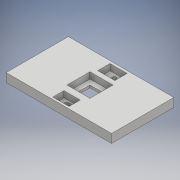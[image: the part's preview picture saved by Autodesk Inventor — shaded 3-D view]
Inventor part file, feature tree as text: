
AUTODESK INVENTOR PART (.ipt)
format: ipt  version: 2017 (Build 210142000, 142)  size: 321,024 bytes
history: native  units: mm
features: extrude x2, sketch x1
ambient origin geometry x8: Origin, YZ Plane, XZ Plane, XY Plane, X Axis, Y Axis, Z Axis, Center Point
bodies: Solido1 (feature_tree)
feature tree (3):
  extrude  "Estrusione1"  Depth=110.0mm
  extrude  "Estrusione4"  Depth=65.0mm
  sketch  "Schizzo2"
